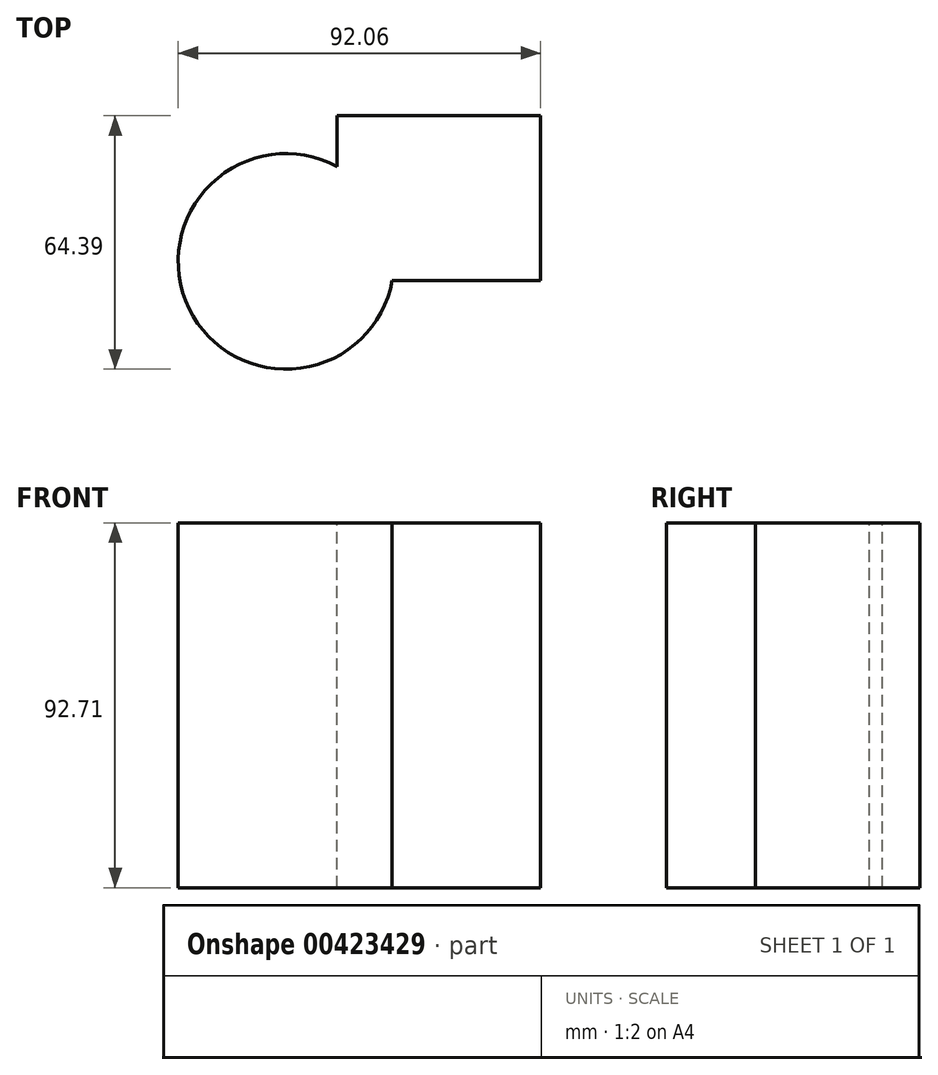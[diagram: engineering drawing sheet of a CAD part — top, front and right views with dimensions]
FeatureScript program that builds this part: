
annotation { "Feature Type Name" : "Feature", "Feature Type Description" : "" }
export const myFeature = defineFeature(function(context is Context, id is Id, definition is map)
    precondition{}
    {
        {
            var Q0;
            Q0=qCreatedBy(makeId("Top.planeOp"),FACE);
            var sketch = newSketch(context, id + "F0", { "sketchPlane" : qUnion([Q0])});
            skCircle(sketch, "E0", {"center": v(-33.09, 28.58) * mm, "radius": 27.4 * mm});
            skLineSegment(sketch, "E1.bottom", {"start": v(-20.15, 65.57) * mm, "end": v(31.58, 65.57) * mm});
            skLineSegment(sketch, "E1.top", {"start": v(-20.15, 23.76) * mm, "end": v(31.58, 23.76) * mm});
            skLineSegment(sketch, "E1.left", {"start": v(-20.15, 65.57) * mm, "end": v(-20.15, 23.76) * mm});
            skLineSegment(sketch, "E1.right", {"start": v(31.58, 65.57) * mm, "end": v(31.58, 23.76) * mm});
            skSolve(sketch);
        }
        {
            var Q0;
            Q0 = qSketchRegion(id + "F0", true);
            extrude(context, id + "F1", {"entities" : qUnion([Q0]), "oppositeDirection" : true, "depth" : 67.3 * mm});
        }
        {
            var Q0;
            Q0 = qSketchRegion(id + "F0", true);
            extrude(context, id + "F2", {"entities" : qUnion([Q0]), "operationType" : NewBodyOperationType.ADD, "depth" : 25.4 * mm});
        }
    });
